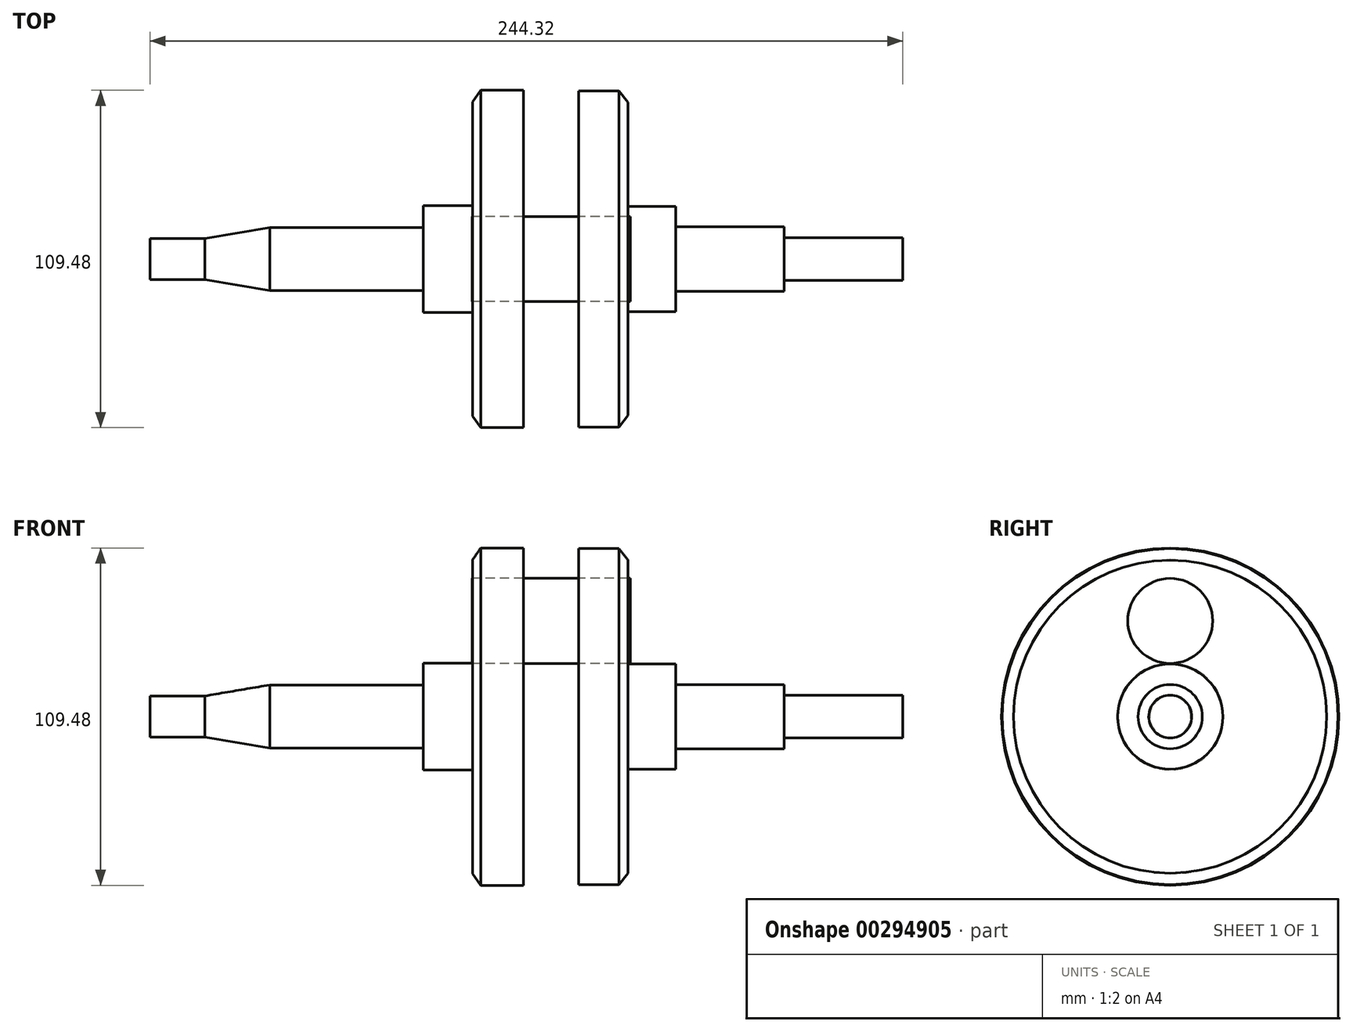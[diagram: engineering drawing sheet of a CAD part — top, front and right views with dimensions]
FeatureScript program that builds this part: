
annotation { "Feature Type Name" : "Feature", "Feature Type Description" : "" }
export const myFeature = defineFeature(function(context is Context, id is Id, definition is map)
    precondition{}
    {
        {
            var Q0;
            Q0=qCreatedBy(makeId("Front.planeOp"),FACE);
            var sketch = newSketch(context, id + "F0", { "sketchPlane" : qUnion([Q0])});
            skLineSegment(sketch, "E0", {"start": v(-456.62, -19.36) * mm, "end": v(-335.47, -19.36) * mm});
            skLineSegment(sketch, "E1", {"start": v(-456.62, -19.36) * mm, "end": v(-456.62, -12.66) * mm});
            skLineSegment(sketch, "E2", {"start": v(-438.76, -12.66) * mm, "end": v(-417.76, -9.08) * mm});
            skLineSegment(sketch, "E3", {"start": v(-417.76, -9.08) * mm, "end": v(-367.97, -9.08) * mm});
            skLineSegment(sketch, "E4", {"start": v(-367.97, -9.08) * mm, "end": v(-367.97, -2.04) * mm});
            skLineSegment(sketch, "E5", {"start": v(-351.9, -2.04) * mm, "end": v(-351.9, 31.58) * mm});
            skLineSegment(sketch, "E6", {"start": v(-351.9, 31.58) * mm, "end": v(-349.26, 35.38) * mm});
            skLineSegment(sketch, "E7", {"start": v(-349.26, 35.38) * mm, "end": v(-335.47, 35.38) * mm});
            skLineSegment(sketch, "E8", {"start": v(-335.47, 35.38) * mm, "end": v(-335.47, -19.36) * mm});
            skLineSegment(sketch, "E9", {"start": v(-367.97, -2.04) * mm, "end": v(-351.9, -2.04) * mm});
            skLineSegment(sketch, "E10", {"start": v(-456.62, -12.66) * mm, "end": v(-438.76, -12.66) * mm});
            skLineSegment(sketch, "E11", {"start": v(-212.3, -19.36) * mm, "end": v(-212.3, -12.38) * mm});
            skLineSegment(sketch, "E12", {"start": v(-212.3, -12.38) * mm, "end": v(-250.77, -12.38) * mm});
            skLineSegment(sketch, "E13", {"start": v(-250.77, -12.38) * mm, "end": v(-250.77, -8.93) * mm});
            skLineSegment(sketch, "E14", {"start": v(-250.77, -8.93) * mm, "end": v(-285.98, -8.93) * mm});
            skLineSegment(sketch, "E15", {"start": v(-285.98, -8.93) * mm, "end": v(-285.98, -2.29) * mm});
            skLineSegment(sketch, "E16", {"start": v(-285.98, -2.29) * mm, "end": v(-301.5, -2.29) * mm});
            skLineSegment(sketch, "E17", {"start": v(-301.5, -2.29) * mm, "end": v(-301.5, 31.44) * mm});
            skLineSegment(sketch, "E18", {"start": v(-301.5, 31.44) * mm, "end": v(-304.45, 35.14) * mm});
            skLineSegment(sketch, "E19", {"start": v(-304.45, 35.14) * mm, "end": v(-317.5, 35.14) * mm});
            skLineSegment(sketch, "E20", {"start": v(-317.5, 35.14) * mm, "end": v(-317.5, -19.36) * mm});
            skLineSegment(sketch, "E21.trimOffspring", {"start": v(-317.5, -19.36) * mm, "end": v(-212.3, -19.36) * mm});
            skLineSegment(sketch, "E22", {"start": v(-301.5, 11.7) * mm, "end": v(-301.5, 25.07) * mm});
            skLineSegment(sketch, "E23", {"start": v(-351.9, 25.07) * mm, "end": v(-351.9, 11.7) * mm});
            skSolve(sketch);
        }
        {
            var Q0;
            Q0=makeQuery(id+"F0.imprint","IMPRINT",FACE,{"disambiguationData":[TD([[makeQuery(id+"F0.imprint","IMPRINT",EDGE,{"derivedFrom":sQuery(id+"F0.wireOp",EDGE,"E0")}),1.0]])]});
            var Q1;
            Q1=sQuery(id+"F0.wireOp",EDGE,"E0");
            revolve(context, id + "F1", {"entities" : qUnion([Q0]), "axis" : qUnion([Q1]), "revolveType" : RevolveType.FULL});
        }
        {
            var Q0;
            Q0=makeQuery(id+"F0.imprint","IMPRINT",FACE,{"disambiguationData":[TD([[makeQuery(id+"F0.imprint","IMPRINT",EDGE,{"derivedFrom":sQuery(id+"F0.wireOp",EDGE,"E11")}),1.0]])]});
            var Q1;
            Q1=sQuery(id+"F0.wireOp",EDGE,"E21.trimOffspring");
            revolve(context, id + "F2", {"entities" : qUnion([Q0]), "axis" : qUnion([Q1]), "revolveType" : RevolveType.FULL});
        }
        {
            var Q0;
            Q0=qCreatedBy(makeId("Front.planeOp"),FACE);
            var sketch = newSketch(context, id + "F3", { "sketchPlane" : qUnion([Q0])});
            skLineSegment(sketch, "E24", {"start": v(-352.09, 11.7) * mm, "end": v(-300.7, 11.7) * mm});
            skLineSegment(sketch, "E25", {"start": v(-300.7, 11.7) * mm, "end": v(-300.7, 25.49) * mm});
            skLineSegment(sketch, "E26", {"start": v(-300.7, 25.49) * mm, "end": v(-352.09, 25.49) * mm});
            skLineSegment(sketch, "E27", {"start": v(-352.09, 25.49) * mm, "end": v(-352.09, 11.7) * mm});
            skSolve(sketch);
        }
        {
            var Q0;
            Q0=makeQuery(id+"F3.imprint","IMPRINT",FACE,{"disambiguationData":[TD([[makeQuery(id+"F3.imprint","IMPRINT",EDGE,{"derivedFrom":sQuery(id+"F3.wireOp",EDGE,"E24")}),1.0]])]});
            var Q1;
            Q1=sQuery(id+"F3.wireOp",EDGE,"E24");
            revolve(context, id + "F4", {"entities" : qUnion([Q0]), "axis" : qUnion([Q1]), "revolveType" : RevolveType.FULL});
        }
    });
